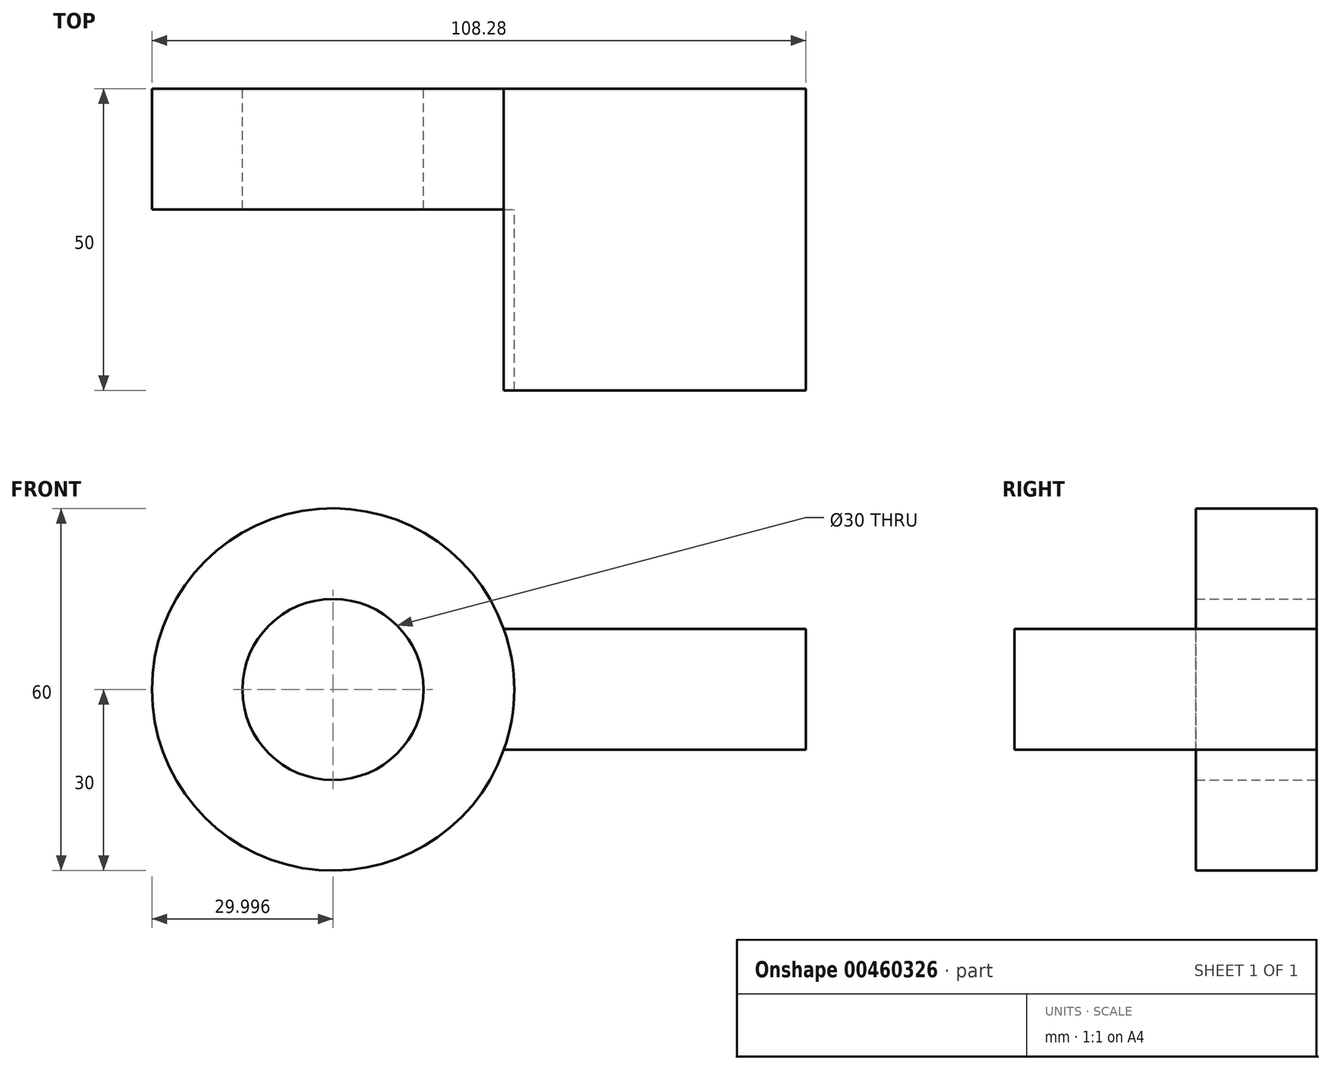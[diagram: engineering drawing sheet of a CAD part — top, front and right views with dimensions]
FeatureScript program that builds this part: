
annotation { "Feature Type Name" : "Feature", "Feature Type Description" : "" }
export const myFeature = defineFeature(function(context is Context, id is Id, definition is map)
    precondition{}
    {
        {
            var Q0;
            Q0=qCreatedBy(makeId("Front.planeOp"),FACE);
            var sketch = newSketch(context, id + "F0", { "sketchPlane" : qUnion([Q0])});
            skCircle(sketch, "E0", {"center": v(-28.28, 0) * mm, "radius": 30 * mm});
            skCircle(sketch, "E1", {"center": v(-28.28, 0) * mm, "radius": 15 * mm});
            skLineSegment(sketch, "E2.bottom", {"start": v(0, 10) * mm, "end": v(50, 10) * mm});
            skLineSegment(sketch, "E2.top", {"start": v(0, -10) * mm, "end": v(50, -10) * mm});
            skLineSegment(sketch, "E2.right", {"start": v(50, 10) * mm, "end": v(50, -10) * mm});
            skPoint(sketch, "E2.middle", {"position": v(25, 0) * mm});
            skSolve(sketch);
        }
        {
            var Q0;
            Q0 = qSketchRegion(id + "F0", true);
            extrude(context, id + "F1", {"entities" : qUnion([Q0]), "depth" : 20 * mm});
        }
        {
            var Q0;
            {var subQ0=sQuery(id+"F0.wireOp",EDGE,"E2.bottom");Q0=makeQuery(id+"F0.imprint","IMPRINT",FACE,{"disambiguationData":[TD([[makeQuery(id+"F0.imprint","IMPRINT",EDGE,{"derivedFrom":subQ0}),-1.0]])]});}
            extrude(context, id + "F2", {"entities" : qUnion([Q0]), "operationType" : NewBodyOperationType.ADD, "depth" : 50 * mm});
        }
    });
